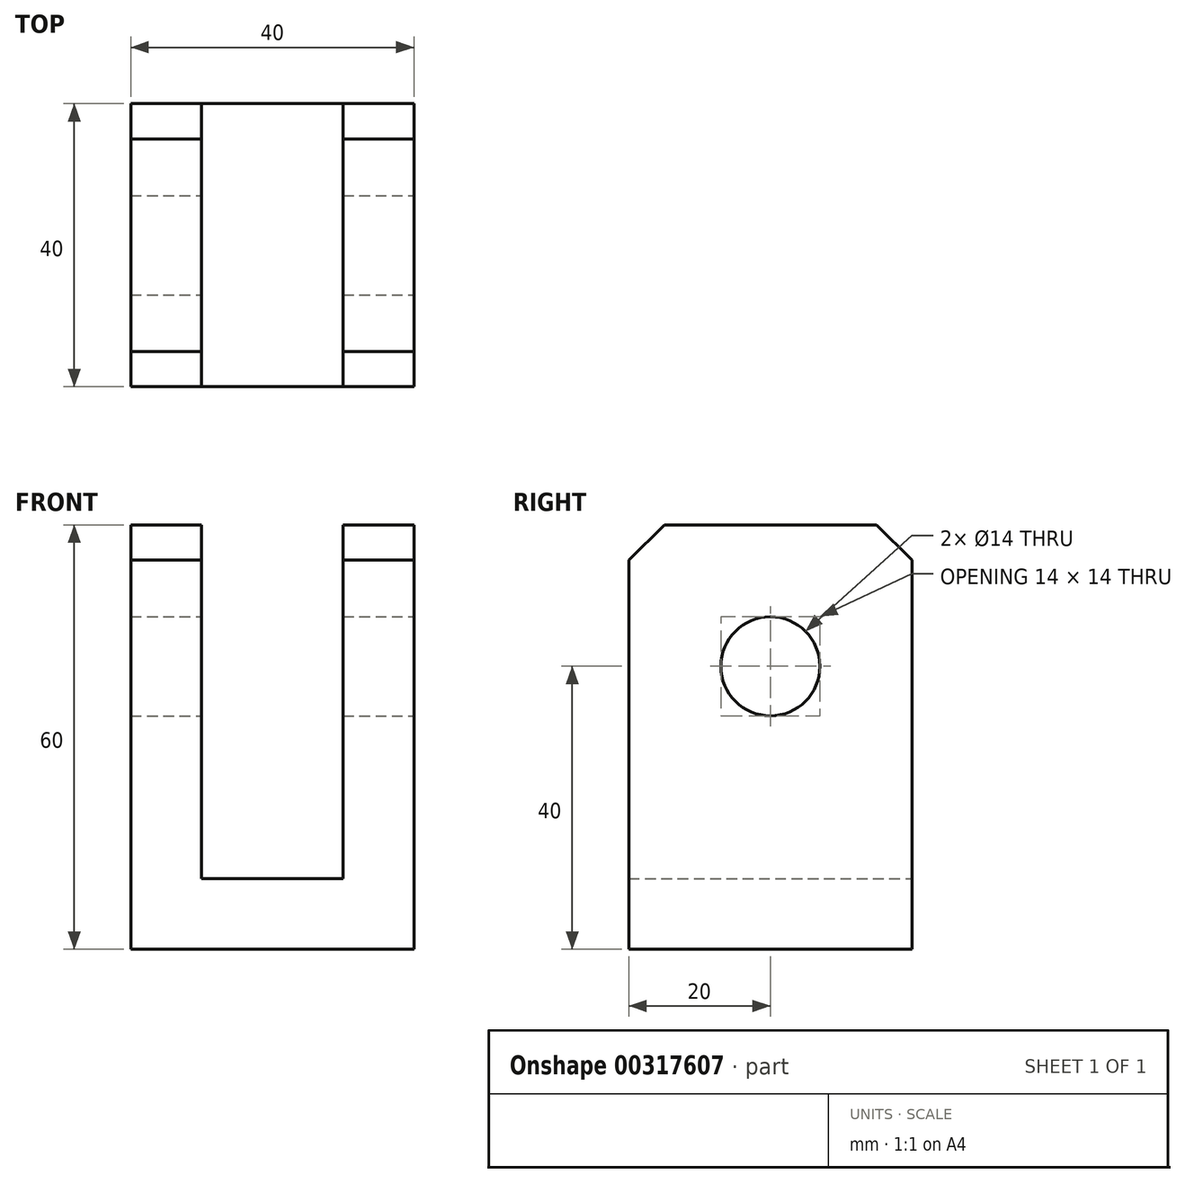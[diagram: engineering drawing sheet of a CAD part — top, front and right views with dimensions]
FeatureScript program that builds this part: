
annotation { "Feature Type Name" : "Feature", "Feature Type Description" : "" }
export const myFeature = defineFeature(function(context is Context, id is Id, definition is map)
    precondition{}
    {
        {
            var Q0;
            Q0=qCreatedBy(makeId("Top.planeOp"),FACE);
            var sketch = newSketch(context, id + "F0", { "sketchPlane" : qUnion([Q0])});
            skLineSegment(sketch, "E0.bottom", {"start": v(-20, 20) * mm, "end": v(20, 20) * mm});
            skLineSegment(sketch, "E0.top", {"start": v(-20, -20) * mm, "end": v(20, -20) * mm});
            skLineSegment(sketch, "E0.left", {"start": v(-20, 20) * mm, "end": v(-20, -20) * mm});
            skLineSegment(sketch, "E0.right", {"start": v(20, 20) * mm, "end": v(20, -20) * mm});
            skSolve(sketch);
        }
        {
            var Q0;
            Q0=makeQuery(id+"F0.imprint","IMPRINT",FACE,{"disambiguationData":[TD([[makeQuery(id+"F0.imprint","IMPRINT",EDGE,{"derivedFrom":sQuery(id+"F0.wireOp",EDGE,"E0.bottom")}),-1.0]])]});
            extrude(context, id + "F1", {"entities" : qUnion([Q0]), "depth" : 10 * mm});
        }
        {
            var Q0;
            Q0=makeQuery(id+"F1.opExtrude","CAP_FACE",FACE,{"disambiguationData":[OSD([sQuery(id+"F0.wireOp",EDGE,"E0.bottom"),sQuery(id+"F0.wireOp",EDGE,"E0.top"),sQuery(id+"F0.wireOp",EDGE,"E0.left"),sQuery(id+"F0.wireOp",EDGE,"E0.right")])],"isStart":false});
            var sketch = newSketch(context, id + "F2", { "sketchPlane" : qUnion([Q0])});
            skLineSegment(sketch, "E1.bottom", {"start": v(-20, -20) * mm, "end": v(-10, -20) * mm});
            skLineSegment(sketch, "E1.top", {"start": v(-20, 20) * mm, "end": v(-10, 20) * mm});
            skLineSegment(sketch, "E1.left", {"start": v(-20, -20) * mm, "end": v(-20, 20) * mm});
            skLineSegment(sketch, "E1.right", {"start": v(-10, -20) * mm, "end": v(-10, 20) * mm});
            skSolve(sketch);
        }
        {
            var Q0;
            Q0=makeQuery(id+"F2.imprint","IMPRINT",FACE,{"disambiguationData":[TD([[makeQuery(id+"F2.imprint","IMPRINT",EDGE,{"derivedFrom":sQuery(id+"F2.wireOp",EDGE,"E1.bottom")}),1.0]])]});
            extrude(context, id + "F3", {"entities" : qUnion([Q0]), "operationType" : NewBodyOperationType.ADD, "depth" : 50 * mm});
        }
        {
            var Q0;
            Q0=makeQuery(id+"F1.opExtrude","CAP_FACE",FACE,{"disambiguationData":[OSD([sQuery(id+"F0.wireOp",EDGE,"E0.bottom"),sQuery(id+"F0.wireOp",EDGE,"E0.top"),sQuery(id+"F0.wireOp",EDGE,"E0.left"),sQuery(id+"F0.wireOp",EDGE,"E0.right")])],"isStart":false});
            var sketch = newSketch(context, id + "F4", { "sketchPlane" : qUnion([Q0])});
            skLineSegment(sketch, "E2.bottom", {"start": v(20, -20) * mm, "end": v(10, -20) * mm});
            skLineSegment(sketch, "E2.top", {"start": v(20, 20) * mm, "end": v(10, 20) * mm});
            skLineSegment(sketch, "E2.left", {"start": v(20, -20) * mm, "end": v(20, 20) * mm});
            skLineSegment(sketch, "E2.right", {"start": v(10, -20) * mm, "end": v(10, 20) * mm});
            skSolve(sketch);
        }
        {
            var Q0;
            Q0=makeQuery(id+"F4.imprint","IMPRINT",FACE,{"disambiguationData":[TD([[makeQuery(id+"F4.imprint","IMPRINT",EDGE,{"derivedFrom":sQuery(id+"F4.wireOp",EDGE,"E2.bottom")}),1.0]])]});
            extrude(context, id + "F5", {"entities" : qUnion([Q0]), "operationType" : NewBodyOperationType.ADD, "depth" : 50 * mm});
        }
        {
            var Q0;
            Q0=makeQuery(id+"F5.boolean.opBoolean","MERGE",FACE,{"derivedFrom":[makeQuery(id+"F1.opExtrude","SWEPT_FACE",FACE,{"disambiguationData":[OSD([sQuery(id+"F0.wireOp",EDGE,"E0.right")])]}),makeQuery(id+"F5.opExtrude","SWEPT_FACE",FACE,{"disambiguationData":[OSD([sQuery(id+"F4.wireOp",EDGE,"E2.left")])]})]});
            var sketch = newSketch(context, id + "F6", { "sketchPlane" : qUnion([Q0])});
            skCircle(sketch, "E3", {"center": v(0, 40) * mm, "radius": 7 * mm});
            skPoint(sketch, "E3.centerSnap0", {"position": v(0, 0) * mm});
            skSolve(sketch);
        }
        {
            var Q0;
            Q0=makeQuery(id+"F6.imprint","IMPRINT",FACE,{"disambiguationData":[TD([[makeQuery(id+"F6.imprint","IMPRINT",EDGE,{"derivedFrom":sQuery(id+"F6.wireOp",EDGE,"E3")}),1.0]])]});
            extrude(context, id + "F7", {"entities" : qUnion([Q0]), "operationType" : NewBodyOperationType.REMOVE, "oppositeDirection" : true, "depth" : 96.2 * mm});
        }
        {
            var Q0;
            Q0=makeQuery(id+"F3.opExtrude","CAP_EDGE",EDGE,{"disambiguationData":[OSD([sQuery(id+"F2.wireOp",EDGE,"E1.bottom")])],"isStart":false});
            var Q1;
            Q1=makeQuery(id+"F5.opExtrude","CAP_EDGE",EDGE,{"disambiguationData":[OSD([sQuery(id+"F4.wireOp",EDGE,"E2.bottom")])],"isStart":false});
            var Q2;
            Q2=makeQuery(id+"F5.opExtrude","CAP_EDGE",EDGE,{"disambiguationData":[OSD([sQuery(id+"F4.wireOp",EDGE,"E2.top")])],"isStart":false});
            var Q3;
            Q3=makeQuery(id+"F3.opExtrude","CAP_EDGE",EDGE,{"disambiguationData":[OSD([sQuery(id+"F2.wireOp",EDGE,"E1.top")])],"isStart":false});
            chamfer(context, id + "F8", {"entities" : qUnion([Q0, Q1, Q2, Q3]), "width" : 5 * mm, "tangentPropagation" : true});
        }
    });
